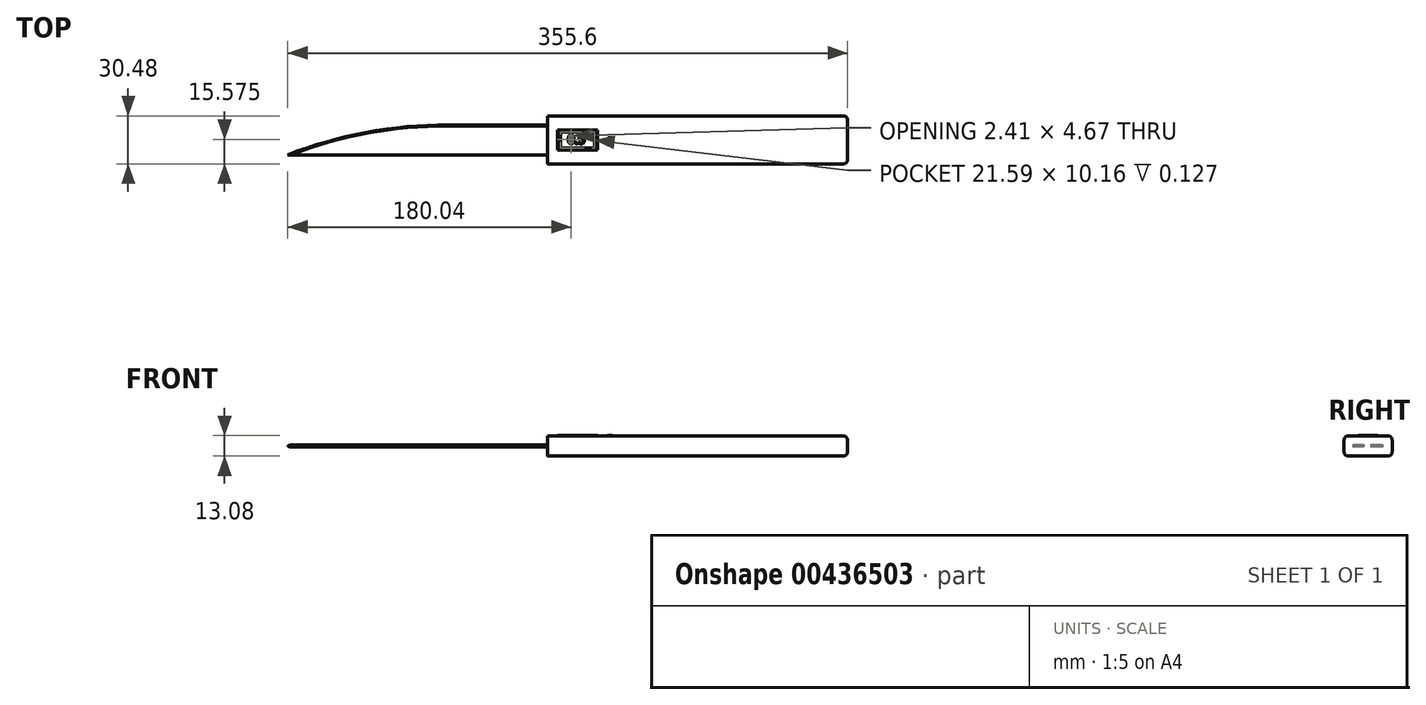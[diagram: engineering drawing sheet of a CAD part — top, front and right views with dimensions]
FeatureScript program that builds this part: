
annotation { "Feature Type Name" : "Feature", "Feature Type Description" : "" }
export const myFeature = defineFeature(function(context is Context, id is Id, definition is map)
    precondition{}
    {
        {
            var Q0;
            Q0=qCreatedBy(makeId("Top.planeOp"),FACE);
            var sketch = newSketch(context, id + "F0", { "sketchPlane" : qUnion([Q0])});
            skLineSegment(sketch, "E0.bottom", {"start": v(0, 15.24) * mm, "end": v(190.5, 15.24) * mm});
            skLineSegment(sketch, "E0.top", {"start": v(0, -15.24) * mm, "end": v(190.5, -15.24) * mm});
            skLineSegment(sketch, "E0.left", {"start": v(0, 15.24) * mm, "end": v(0, -15.24) * mm});
            skLineSegment(sketch, "E0.right", {"start": v(190.5, 15.24) * mm, "end": v(190.5, -15.24) * mm});
            skSolve(sketch);
        }
        {
            var Q0;
            Q0=makeQuery(id+"F0.imprint","IMPRINT",FACE,{"disambiguationData":[TD([[makeQuery(id+"F0.imprint","IMPRINT",EDGE,{"derivedFrom":sQuery(id+"F0.wireOp",EDGE,"E0.bottom")}),-1.0]])]});
            extrude(context, id + "F1", {"entities" : qUnion([Q0]), "depth" : 6.35 * mm, "hasSecondDirection" : true, "secondDirectionOppositeDirection" : true, "secondDirectionDepth" : 6.35 * mm});
        }
        {
            var Q0;
            Q0=qCreatedBy(makeId("Top.planeOp"),FACE);
            var sketch = newSketch(context, id + "F2", { "sketchPlane" : qUnion([Q0])});
            skLineSegment(sketch, "E1", {"start": v(0, 9.52) * mm, "end": v(0, -9.53) * mm});
            skLineSegment(sketch, "E2", {"start": v(0, -9.53) * mm, "end": v(-165.1, -9.53) * mm});
            skLineSegment(sketch, "E3", {"start": v(0, 9.52) * mm, "end": v(-63.5, 9.52) * mm});
            skArc(sketch, "E4", {"start": v(-63.5, 9.53) * mm, "mid": v(-115.19, 4.72) * mm, "end": v(-165.1, -9.53) * mm});
            skSolve(sketch);
        }
        {
            var Q0;
            Q0=makeQuery(id+"F2.imprint","IMPRINT",FACE,{"disambiguationData":[TD([[makeQuery(id+"F2.imprint","IMPRINT",EDGE,{"derivedFrom":sQuery(id+"F2.wireOp",EDGE,"E1")}),-1.0]])]});
            extrude(context, id + "F3", {"entities" : qUnion([Q0]), "depth" : 0.64 * mm, "hasSecondDirection" : true, "secondDirectionOppositeDirection" : true, "secondDirectionDepth" : 0.64 * mm});
        }
        {
            var Q0;
            Q0=makeQuery(id+"F1.opExtrude","CAP_EDGE",EDGE,{"disambiguationData":[OSD([sQuery(id+"F0.wireOp",EDGE,"E0.top")])],"isStart":false});
            var Q1;
            Q1=makeQuery(id+"F1.opExtrude","CAP_EDGE",EDGE,{"disambiguationData":[OSD([sQuery(id+"F0.wireOp",EDGE,"E0.top")])],"isStart":true});
            var Q2;
            Q2=makeQuery(id+"F1.opExtrude","SWEPT_EDGE",EDGE,{"disambiguationData":[OSD([sQuery(id+"F0.wireOp",EDGE,"E0.top"),sQuery(id+"F0.wireOp",EDGE,"E0.right")])]});
            var Q3;
            Q3=makeQuery(id+"F1.opExtrude","SWEPT_EDGE",EDGE,{"disambiguationData":[OSD([sQuery(id+"F0.wireOp",EDGE,"E0.bottom"),sQuery(id+"F0.wireOp",EDGE,"E0.right")])]});
            var Q4;
            Q4=makeQuery(id+"F1.opExtrude","CAP_EDGE",EDGE,{"disambiguationData":[OSD([sQuery(id+"F0.wireOp",EDGE,"E0.bottom")])],"isStart":false});
            var Q5;
            Q5=makeQuery(id+"F1.opExtrude","CAP_EDGE",EDGE,{"disambiguationData":[OSD([sQuery(id+"F0.wireOp",EDGE,"E0.right")])],"isStart":true});
            var Q6;
            Q6=makeQuery(id+"F1.opExtrude","CAP_EDGE",EDGE,{"disambiguationData":[OSD([sQuery(id+"F0.wireOp",EDGE,"E0.bottom")])],"isStart":true});
            var Q7;
            Q7=makeQuery(id+"F1.opExtrude","CAP_EDGE",EDGE,{"disambiguationData":[OSD([sQuery(id+"F0.wireOp",EDGE,"E0.right")])],"isStart":false});
            fillet(context, id + "F4", {"entities" : qUnion([Q0, Q1, Q2, Q3, Q4, Q5, Q6, Q7]), "radius" : 2.54 * mm, "tangentPropagation" : true, "allowEdgeOverflow" : false});
        }
        {
            var Q0;
            Q0=makeQuery(id+"F3.opExtrude","CAP_EDGE",EDGE,{"disambiguationData":[OSD([sQuery(id+"F2.wireOp",EDGE,"E4")])],"isStart":false});
            var Q1;
            Q1=makeQuery(id+"F3.opExtrude","CAP_EDGE",EDGE,{"disambiguationData":[OSD([sQuery(id+"F2.wireOp",EDGE,"E4")])],"isStart":true});
            var Q2;
            Q2=makeQuery(id+"F3.opExtrude","CAP_EDGE",EDGE,{"disambiguationData":[OSD([sQuery(id+"F2.wireOp",EDGE,"E3")])],"isStart":true});
            var Q3;
            Q3=makeQuery(id+"F3.opExtrude","SWEPT_FACE",FACE,{"disambiguationData":[OSD([sQuery(id+"F2.wireOp",EDGE,"E3")])]});
            chamfer(context, id + "F5", {"entities" : qUnion([Q0, Q1, Q2, Q3]), "width" : 0.64 * mm, "tangentPropagation" : true});
        }
        {
            var Q0;
            Q0=makeQuery(id+"F1.opExtrude","CAP_FACE",FACE,{"disambiguationData":[OSD([sQuery(id+"F0.wireOp",EDGE,"E0.bottom"),sQuery(id+"F0.wireOp",EDGE,"E0.top"),sQuery(id+"F0.wireOp",EDGE,"E0.left"),sQuery(id+"F0.wireOp",EDGE,"E0.right")])],"isStart":false});
            var sketch = newSketch(context, id + "F6", { "sketchPlane" : qUnion([Q0])});
            skLineSegment(sketch, "E5.bottom", {"start": v(6.35, 6.35) * mm, "end": v(31.75, 6.35) * mm});
            skLineSegment(sketch, "E5.top", {"start": v(6.35, -6.35) * mm, "end": v(31.75, -6.35) * mm});
            skLineSegment(sketch, "E5.left", {"start": v(6.35, 6.35) * mm, "end": v(6.35, -6.35) * mm});
            skLineSegment(sketch, "E5.right", {"start": v(31.75, 6.35) * mm, "end": v(31.75, -6.35) * mm});
            skSolve(sketch);
        }
        {
            var Q0;
            Q0=makeQuery(id+"F6.imprint","IMPRINT",FACE,{"disambiguationData":[TD([[makeQuery(id+"F6.imprint","IMPRINT",EDGE,{"derivedFrom":sQuery(id+"F6.wireOp",EDGE,"E5.bottom")}),-1.0]])]});
            extrude(context, id + "F7", {"entities" : qUnion([Q0]), "operationType" : NewBodyOperationType.ADD, "depth" : 0.25 * mm});
        }
        {
            var Q0;
            Q0=makeQuery(id+"F1.opExtrude","CAP_FACE",FACE,{"disambiguationData":[OSD([sQuery(id+"F0.wireOp",EDGE,"E0.bottom"),sQuery(id+"F0.wireOp",EDGE,"E0.top"),sQuery(id+"F0.wireOp",EDGE,"E0.left"),sQuery(id+"F0.wireOp",EDGE,"E0.right")])],"isStart":false});
            var sketch = newSketch(context, id + "F8", { "sketchPlane" : qUnion([Q0])});
            skCircle(sketch, "E6", {"center": v(39.69, 0) * mm, "radius": 1.59 * mm});
            skSolve(sketch);
        }
        {
            var Q0;
            Q0=makeQuery(id+"F8.imprint","IMPRINT",FACE,{"disambiguationData":[TD([[makeQuery(id+"F8.imprint","IMPRINT",EDGE,{"derivedFrom":sQuery(id+"F8.wireOp",EDGE,"E6")}),1.0]])]});
            extrude(context, id + "F9", {"entities" : qUnion([Q0]), "depth" : 0.38 * mm});
        }
        {
            var Q0;
            Q0=makeQuery(id+"F9.opExtrude","CAP_EDGE",EDGE,{"disambiguationData":[OSD([sQuery(id+"F8.wireOp",EDGE,"E6")])],"isStart":false});
            fillet(context, id + "F10", {"entities" : qUnion([Q0]), "radius" : 0.13 * mm, "tangentPropagation" : true, "allowEdgeOverflow" : false});
        }
        {
            var Q0;
            Q0=makeQuery(id+"F7.opExtrude","CAP_FACE",FACE,{"disambiguationData":[OSD([sQuery(id+"F6.wireOp",EDGE,"E5.bottom"),sQuery(id+"F6.wireOp",EDGE,"E5.top"),sQuery(id+"F6.wireOp",EDGE,"E5.left"),sQuery(id+"F6.wireOp",EDGE,"E5.right")])],"isStart":false});
            var sketch = newSketch(context, id + "F11", { "sketchPlane" : qUnion([Q0])});
            skLineSegment(sketch, "E7.bottom", {"start": v(8.26, 5.08) * mm, "end": v(29.85, 5.08) * mm});
            skLineSegment(sketch, "E7.top", {"start": v(8.26, -5.08) * mm, "end": v(29.85, -5.08) * mm});
            skLineSegment(sketch, "E7.left", {"start": v(8.25, 5.08) * mm, "end": v(8.25, -5.08) * mm});
            skLineSegment(sketch, "E7.right", {"start": v(29.84, 5.08) * mm, "end": v(29.84, -5.08) * mm});
            skSolve(sketch);
        }
        {
            var Q0;
            Q0=makeQuery(id+"F11.imprint","IMPRINT",FACE,{"disambiguationData":[TD([[makeQuery(id+"F11.imprint","IMPRINT",EDGE,{"derivedFrom":sQuery(id+"F11.wireOp",EDGE,"E7.bottom")}),-1.0]])]});
            extrude(context, id + "F12", {"entities" : qUnion([Q0]), "operationType" : NewBodyOperationType.REMOVE, "oppositeDirection" : true, "depth" : 0.13 * mm});
        }
        {
            var Q0;
            Q0=makeQuery(id+"F12.boolean.opBoolean","COPY",FACE,{"derivedFrom":makeQuery(id+"F12.opExtrude","CAP_FACE",FACE,{"disambiguationData":[OSD([sQuery(id+"F11.wireOp",EDGE,"E7.bottom"),sQuery(id+"F11.wireOp",EDGE,"E7.top"),sQuery(id+"F11.wireOp",EDGE,"E7.left"),sQuery(id+"F11.wireOp",EDGE,"E7.right")])],"isStart":false})});
            var sketch = newSketch(context, id + "F13", { "sketchPlane" : qUnion([Q0])});
            skText(sketch, "E8", { "text": "0.5\n", "fontName": "OpenSans-Regular.ttf"});
            const initialGuessF13  = {"E8": [0.0127, -0.00247, 1, 0, 0.00565]};
            skSetInitialGuess(sketch, initialGuessF13);
            skSolve(sketch);
        }
        {
            var Q0;
            Q0 = qSketchRegion(id + "F13", true);
            extrude(context, id + "F14", {"entities" : qUnion([Q0]), "depth" : 0.13 * mm});
        }
    });
